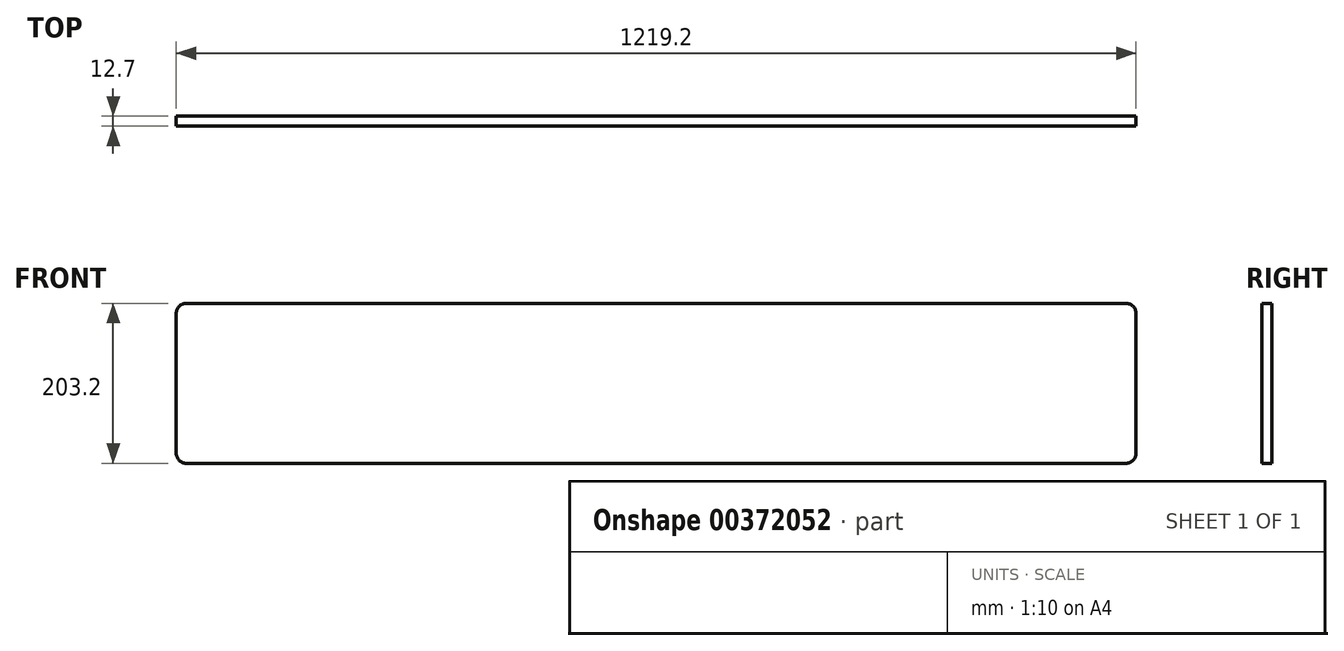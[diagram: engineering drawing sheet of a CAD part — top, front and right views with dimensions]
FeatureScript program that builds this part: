
annotation { "Feature Type Name" : "Feature", "Feature Type Description" : "" }
export const myFeature = defineFeature(function(context is Context, id is Id, definition is map)
    precondition{}
    {
        {
            var Q0;
            Q0=qCreatedBy(makeId("Front.planeOp"),FACE);
            var sketch = newSketch(context, id + "F0", { "sketchPlane" : qUnion([Q0])});
            skLineSegment(sketch, "E0.bottom", {"start": v(-565.68, -85.28) * mm, "end": v(628.12, -85.28) * mm});
            skLineSegment(sketch, "E0.top", {"start": v(-565.68, 117.92) * mm, "end": v(628.12, 117.92) * mm});
            skLineSegment(sketch, "E0.left", {"start": v(-578.38, -72.58) * mm, "end": v(-578.38, 105.22) * mm});
            skLineSegment(sketch, "E0.right", {"start": v(640.82, -72.58) * mm, "end": v(640.82, 105.22) * mm});
            skPoint(sketch, "E1.visualSharp", {"position": v(-578.38, 117.92) * mm});
            skArc(sketch, "E1.filletArc", {"start": v(-565.68, 117.92) * mm, "mid": v(-574.66, 114.2) * mm, "end": v(-578.38, 105.22) * mm});
            skPoint(sketch, "E2.visualSharp", {"position": v(-578.38, -85.28) * mm});
            skArc(sketch, "E2.filletArc", {"start": v(-578.38, -72.58) * mm, "mid": v(-574.66, -81.56) * mm, "end": v(-565.68, -85.28) * mm});
            skPoint(sketch, "E3.visualSharp", {"position": v(640.82, -85.28) * mm});
            skArc(sketch, "E3.filletArc", {"start": v(628.12, -85.28) * mm, "mid": v(637.1, -81.56) * mm, "end": v(640.82, -72.58) * mm});
            skPoint(sketch, "E4.visualSharp", {"position": v(640.82, 117.92) * mm});
            skArc(sketch, "E4.filletArc", {"start": v(640.82, 105.22) * mm, "mid": v(637.1, 114.2) * mm, "end": v(628.12, 117.92) * mm});
            skSolve(sketch);
        }
        {
            var Q0;
            Q0 = qSketchRegion(id + "F0", true);
            extrude(context, id + "F1", {"entities" : qUnion([Q0]), "depth" : 12.7 * mm});
        }
    });
